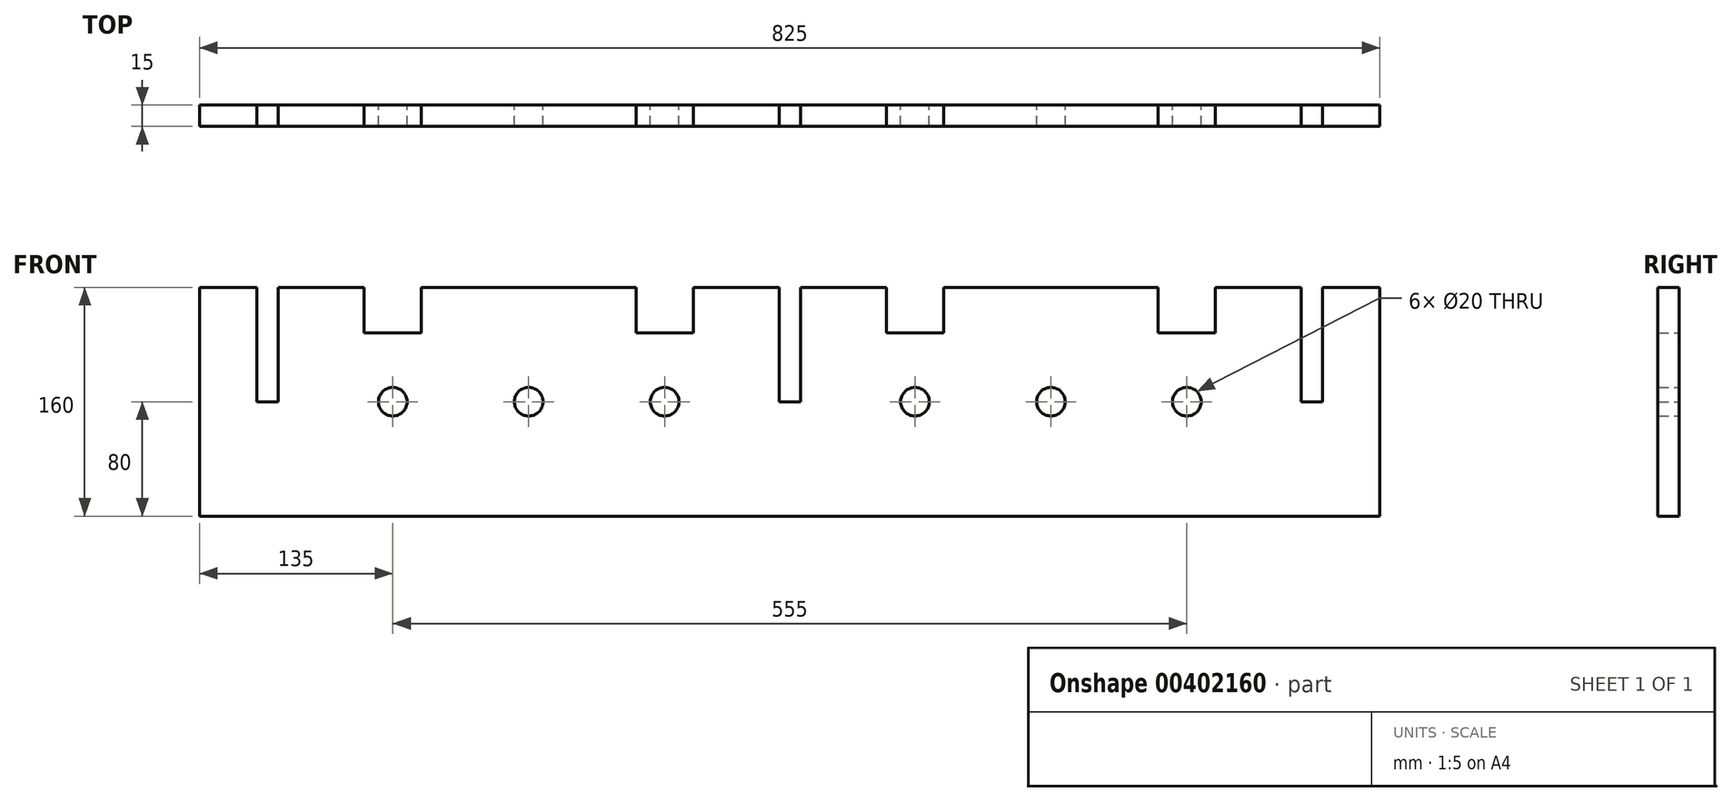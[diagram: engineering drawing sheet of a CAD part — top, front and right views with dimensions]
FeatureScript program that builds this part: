
annotation { "Feature Type Name" : "Feature", "Feature Type Description" : "" }
export const myFeature = defineFeature(function(context is Context, id is Id, definition is map)
    precondition{}
    {
        {
            var Q0;
            Q0=qCreatedBy(makeId("Front.planeOp"),FACE);
            var sketch = newSketch(context, id + "F0", { "sketchPlane" : qUnion([Q0])});
            skLineSegment(sketch, "E0.bottom", {"start": v(-412.5, 80) * mm, "end": v(-372.5, 80) * mm});
            skLineSegment(sketch, "E0.top", {"start": v(-412.5, -80) * mm, "end": v(412.5, -80) * mm});
            skLineSegment(sketch, "E0.left", {"start": v(-412.5, 80) * mm, "end": v(-412.5, -80) * mm});
            skLineSegment(sketch, "E0.right", {"start": v(412.5, 80) * mm, "end": v(412.5, -80) * mm});
            skLineSegment(sketch, "E1", {"start": v(-372.5, 80) * mm, "end": v(-372.5, 0) * mm});
            skLineSegment(sketch, "E2", {"start": v(-372.5, 0) * mm, "end": v(-357.5, 0) * mm});
            skLineSegment(sketch, "E3", {"start": v(-357.5, 0) * mm, "end": v(-357.5, 80) * mm});
            skLineSegment(sketch, "E4.trimOffspring", {"start": v(-357.5, 80) * mm, "end": v(-297.5, 80) * mm});
            skLineSegment(sketch, "E5.top", {"start": v(372.5, 0) * mm, "end": v(357.5, 0) * mm});
            skLineSegment(sketch, "E5.left", {"start": v(372.5, 80) * mm, "end": v(372.5, 0) * mm});
            skLineSegment(sketch, "E5.right", {"start": v(357.5, 80) * mm, "end": v(357.5, 0) * mm});
            skLineSegment(sketch, "E6.top", {"start": v(-7.5, 0) * mm, "end": v(7.5, 0) * mm});
            skLineSegment(sketch, "E6.left", {"start": v(-7.5, 80) * mm, "end": v(-7.5, 0) * mm});
            skLineSegment(sketch, "E6.right", {"start": v(7.5, 80) * mm, "end": v(7.5, 0) * mm});
            skLineSegment(sketch, "E7.trimOffspring", {"start": v(7.5, 80) * mm, "end": v(67.5, 80) * mm});
            skLineSegment(sketch, "E8.trimOffspring", {"start": v(372.5, 80) * mm, "end": v(412.5, 80) * mm});
            skLineSegment(sketch, "E9", {"start": v(-297.5, 80) * mm, "end": v(-297.5, 48) * mm});
            skLineSegment(sketch, "E10", {"start": v(-297.5, 48) * mm, "end": v(-257.5, 48) * mm});
            skLineSegment(sketch, "E11", {"start": v(-257.5, 48) * mm, "end": v(-257.5, 80) * mm});
            skLineSegment(sketch, "E12", {"start": v(-107.5, 80) * mm, "end": v(-107.5, 48) * mm});
            skLineSegment(sketch, "E13", {"start": v(-107.5, 48) * mm, "end": v(-67.5, 48) * mm});
            skLineSegment(sketch, "E14", {"start": v(-67.5, 48) * mm, "end": v(-67.5, 80) * mm});
            skLineSegment(sketch, "E15", {"start": v(67.5, 80) * mm, "end": v(67.5, 48) * mm});
            skLineSegment(sketch, "E16", {"start": v(67.5, 48) * mm, "end": v(107.5, 48) * mm});
            skLineSegment(sketch, "E17", {"start": v(107.5, 48) * mm, "end": v(107.5, 80) * mm});
            skLineSegment(sketch, "E18", {"start": v(257.5, 80) * mm, "end": v(257.5, 48) * mm});
            skLineSegment(sketch, "E19", {"start": v(257.5, 48) * mm, "end": v(297.5, 48) * mm});
            skLineSegment(sketch, "E20", {"start": v(297.5, 48) * mm, "end": v(297.5, 80) * mm});
            skLineSegment(sketch, "E21.trimOffspring", {"start": v(-257.5, 80) * mm, "end": v(-107.5, 80) * mm});
            skLineSegment(sketch, "E22.trimOffspring", {"start": v(-67.5, 80) * mm, "end": v(-7.5, 80) * mm});
            skLineSegment(sketch, "E23.trimOffspring", {"start": v(107.5, 80) * mm, "end": v(257.5, 80) * mm});
            skLineSegment(sketch, "E24.trimOffspring", {"start": v(297.5, 80) * mm, "end": v(357.5, 80) * mm});
            skPoint(sketch, "E25.centerSnap0", {"position": v(-277.5, 48) * mm});
            skCircle(sketch, "E26", {"center": v(-87.5, 0) * mm, "radius": 10 * mm});
            skPoint(sketch, "E26.centerSnap0", {"position": v(-87.5, 48) * mm});
            skCircle(sketch, "E27", {"center": v(87.5, 0) * mm, "radius": 10 * mm});
            skPoint(sketch, "E27.centerSnap0", {"position": v(87.5, 48) * mm});
            skCircle(sketch, "E28", {"center": v(277.5, 0) * mm, "radius": 10 * mm});
            skPoint(sketch, "E28.centerSnap0", {"position": v(277.5, 48) * mm});
            skCircle(sketch, "E29", {"center": v(182.5, 0) * mm, "radius": 10 * mm});
            skPoint(sketch, "E29.centerSnap0", {"position": v(182.5, 80) * mm});
            skCircle(sketch, "E30", {"center": v(-182.5, 0) * mm, "radius": 10 * mm});
            skPoint(sketch, "E30.centerSnap0", {"position": v(-182.5, 80) * mm});
            skCircle(sketch, "E31", {"center": v(-277.5, 0) * mm, "radius": 10 * mm});
            skLineSegment(sketch, "E32", {"start": v(-412.5, -80) * mm, "end": v(-332.5, -80) * mm});
            skLineSegment(sketch, "E33", {"start": v(412.5, -80) * mm, "end": v(332.5, -80) * mm});
            skSolve(sketch);
        }
        {
            var Q0;
            Q0=makeQuery(id+"F0.imprint","IMPRINT",FACE,{"disambiguationData":[TD([[makeQuery(id+"F0.imprint","IMPRINT",EDGE,{"derivedFrom":sQuery(id+"F0.wireOp",EDGE,"E0.bottom")}),-1.0]])]});
            extrude(context, id + "F1", {"entities" : qUnion([Q0]), "depth" : 15 * mm});
        }
    });
